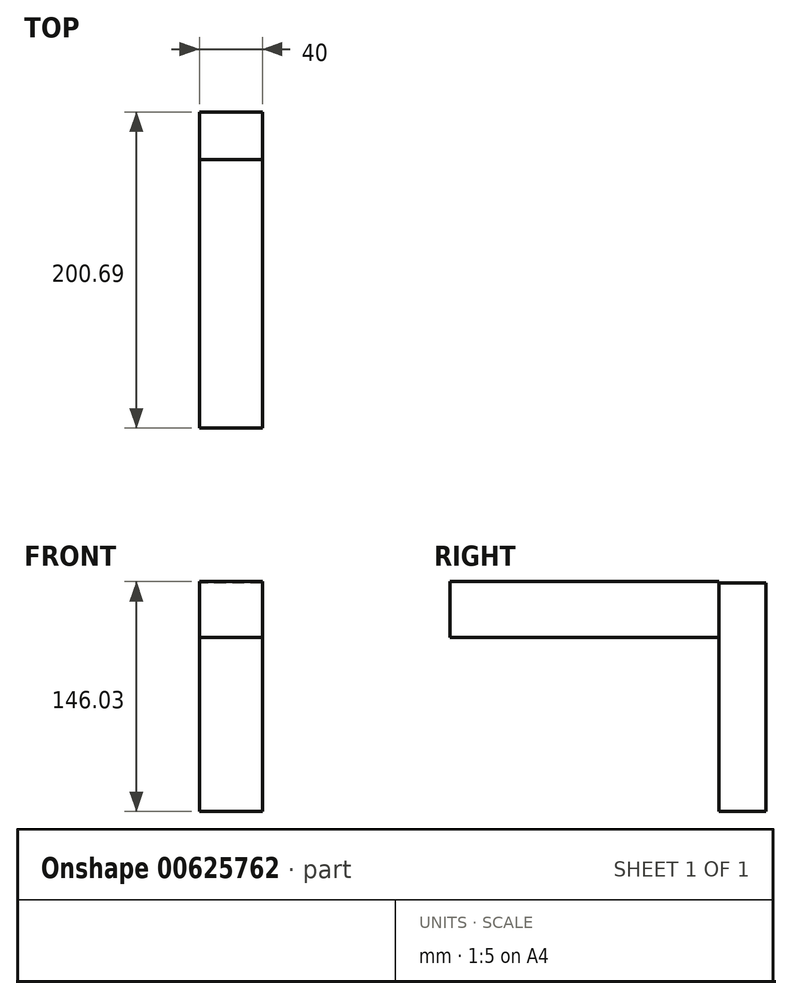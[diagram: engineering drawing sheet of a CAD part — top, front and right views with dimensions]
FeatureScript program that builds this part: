
annotation { "Feature Type Name" : "Feature", "Feature Type Description" : "" }
export const myFeature = defineFeature(function(context is Context, id is Id, definition is map)
    precondition{}
    {
        {
            var Q0;
            Q0=qCreatedBy(makeId("Right.planeOp"),FACE);
            var sketch = newSketch(context, id + "F0", { "sketchPlane" : qUnion([Q0])});
            skLineSegment(sketch, "E0.bottom", {"start": v(-15, 72.5) * mm, "end": v(15, 72.5) * mm});
            skLineSegment(sketch, "E0.top", {"start": v(-15, -72.5) * mm, "end": v(15, -72.5) * mm});
            skLineSegment(sketch, "E0.left", {"start": v(-15, 72.5) * mm, "end": v(-15, -72.5) * mm});
            skLineSegment(sketch, "E0.right", {"start": v(15, 72.5) * mm, "end": v(15, -72.5) * mm});
            skPoint(sketch, "E0.middle", {"position": v(0, 0) * mm});
            skSolve(sketch);
        }
        {
            var Q0;
            Q0=makeQuery(id+"F0.imprint","IMPRINT",FACE,{"disambiguationData":[TD([[makeQuery(id+"F0.imprint","IMPRINT",EDGE,{"derivedFrom":sQuery(id+"F0.wireOp",EDGE,"E0.bottom")}),-1.0]])]});
            extrude(context, id + "F1", {"entities" : qUnion([Q0]), "depth" : 40 * mm, "offsetDistance" : 25 * mm});
        }
        {
            var Q0;
            Q0=qCreatedBy(makeId("Right.planeOp"),FACE);
            var sketch = newSketch(context, id + "F2", { "sketchPlane" : qUnion([Q0])});
            skLineSegment(sketch, "E1.bottom", {"start": v(-15, 73.53) * mm, "end": v(-185.69, 73.53) * mm});
            skLineSegment(sketch, "E1.top", {"start": v(-15, 38.12) * mm, "end": v(-185.69, 38.12) * mm});
            skLineSegment(sketch, "E1.left", {"start": v(-15, 73.53) * mm, "end": v(-15, 38.12) * mm});
            skLineSegment(sketch, "E1.right", {"start": v(-185.69, 73.53) * mm, "end": v(-185.69, 38.12) * mm});
            skSolve(sketch);
        }
        {
            var Q0;
            Q0=makeQuery(id+"F2.imprint","IMPRINT",FACE,{"disambiguationData":[TD([[makeQuery(id+"F2.imprint","IMPRINT",EDGE,{"derivedFrom":sQuery(id+"F2.wireOp",EDGE,"E1.bottom")}),1.0]])]});
            extrude(context, id + "F3", {"entities" : qUnion([Q0]), "depth" : 40 * mm, "offsetDistance" : 25 * mm});
        }
    });
